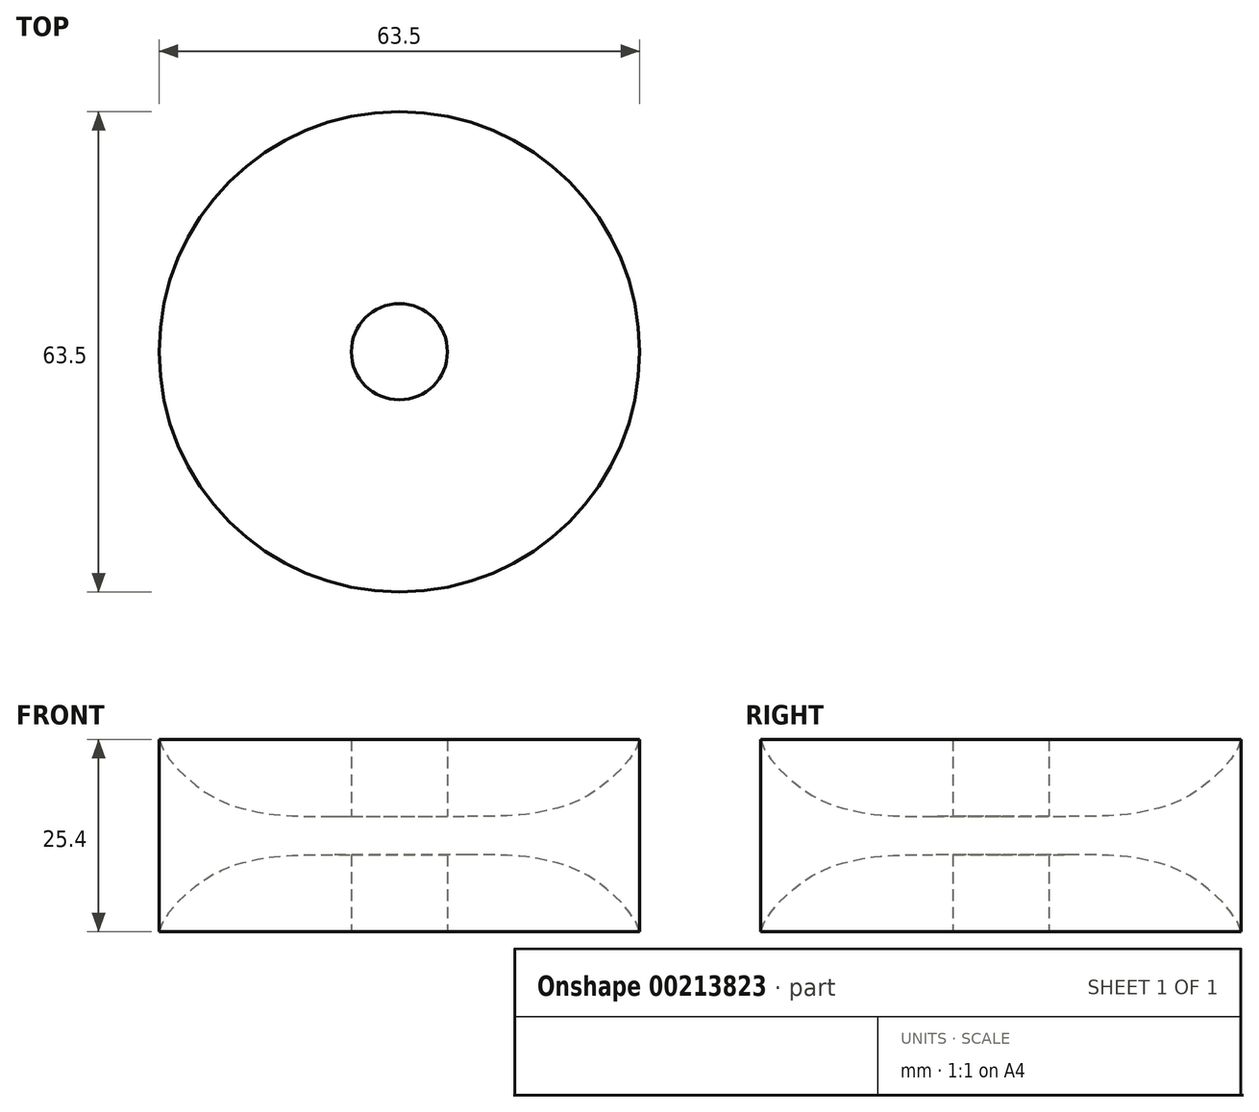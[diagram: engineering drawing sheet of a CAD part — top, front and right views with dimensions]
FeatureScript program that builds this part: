
annotation { "Feature Type Name" : "Feature", "Feature Type Description" : "" }
export const myFeature = defineFeature(function(context is Context, id is Id, definition is map)
    precondition{}
    {
        {
            var Q0;
            Q0=qCreatedBy(makeId("Front.planeOp"),FACE);
            var sketch = newSketch(context, id + "F0", { "sketchPlane" : qUnion([Q0])});
            skLineSegment(sketch, "E0", {"start": v(31.75, 0) * mm, "end": v(31.75, 12.7) * mm});
            skFitSpline(sketch, "E1", {"points": [v(31.75, 12.7) * mm, v(26.61, 6.43) * mm, v(22.33, 4.09) * mm, v(19.29, 3.25) * mm, v(15.32, 2.67) * mm, v(9.85, 2.54) * mm, v(4.43, 2.54) * mm], "startDerivative": vector(-7.1, -30.97) * mm, "endDerivative": vector(-28.91, 0.06) * mm});
            skLineSegment(sketch, "E2", {"start": v(4.43, 2.54) * mm, "end": v(0, 2.54) * mm});
            skLineSegment(sketch, "E3.MirrorCS", {"start": v(31.75, 0) * mm, "end": v(31.75, -12.7) * mm});
            skFitSpline(sketch, "E4.MirrorCS", {"points": [v(31.75, -12.7) * mm, v(26.61, -6.43) * mm, v(22.33, -4.09) * mm, v(19.29, -3.25) * mm, v(15.32, -2.67) * mm, v(9.85, -2.54) * mm, v(4.43, -2.54) * mm], "startDerivative": vector(-7.1, 30.97) * mm, "endDerivative": vector(-28.91, -0.06) * mm});
            skLineSegment(sketch, "E5.MirrorCS", {"start": v(4.43, -2.54) * mm, "end": v(0, -2.54) * mm});
            skLineSegment(sketch, "E6", {"start": v(0, -2.54) * mm, "end": v(0, 2.54) * mm});
            skSolve(sketch);
        }
        {
            var Q0;
            Q0=makeQuery(id+"F0.imprint","IMPRINT",FACE,{"disambiguationData":[TD([[makeQuery(id+"F0.imprint","IMPRINT",EDGE,{"derivedFrom":sQuery(id+"F0.wireOp",EDGE,"E0")}),1.0]])]});
            var Q1;
            Q1=sQuery(id+"F0.wireOp",EDGE,"E6");
            revolve(context, id + "F1", {"entities" : qUnion([Q0]), "axis" : qUnion([Q1]), "revolveType" : RevolveType.FULL});
        }
        {
            var Q0;
            Q0=qCreatedBy(makeId("Top.planeOp"),FACE);
            var sketch = newSketch(context, id + "F2", { "sketchPlane" : qUnion([Q0])});
            skCircle(sketch, "E7", {"center": v(0, 0) * mm, "radius": 6.35 * mm});
            skSolve(sketch);
        }
        {
            var Q0;
            Q0 = qSketchRegion(id + "F2", true);
            extrude(context, id + "F3", {"entities" : qUnion([Q0]), "operationType" : NewBodyOperationType.ADD, "endBound" : BoundingType.SYMMETRIC, "depth" : 25.4 * mm});
        }
    });
